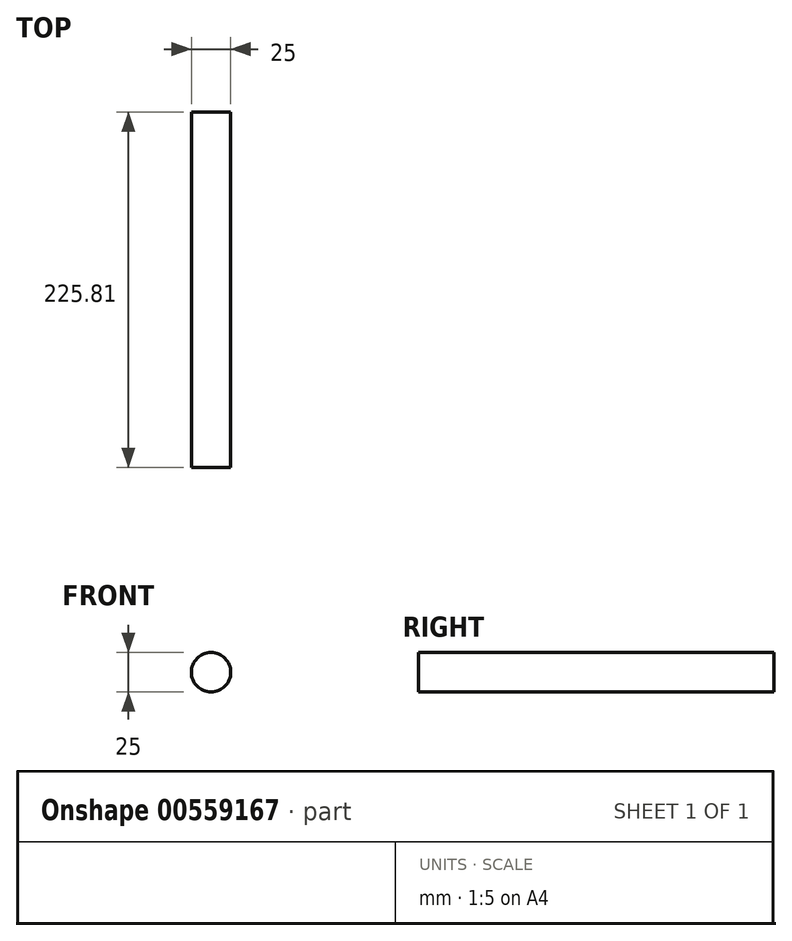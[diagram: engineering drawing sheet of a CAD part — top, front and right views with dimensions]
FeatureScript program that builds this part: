
annotation { "Feature Type Name" : "Feature", "Feature Type Description" : "" }
export const myFeature = defineFeature(function(context is Context, id is Id, definition is map)
    precondition{}
    {
        {
            var Q0;
            Q0=qCreatedBy(makeId("Front.planeOp"),FACE);
            var sketch = newSketch(context, id + "F0", { "sketchPlane" : qUnion([Q0])});
            skCircle(sketch, "E0", {"center": v(-125.22, 56.1) * mm, "radius": 12.5 * mm});
            skSolve(sketch);
        }
        {
            var Q0;
            Q0=makeQuery(id+"F0.imprint","IMPRINT",FACE,{"disambiguationData":[TD([[makeQuery(id+"F0.imprint","IMPRINT",EDGE,{"derivedFrom":sQuery(id+"F0.wireOp",EDGE,"E0")}),1.0]])]});
            extrude(context, id + "F1", {"entities" : qUnion([Q0]), "depth" : 225.8 * mm, "offsetDistance" : 25.4 * mm});
        }
        {
            var Q0;
            Q0=qCreatedBy(makeId("Right.planeOp"),FACE);
            var sketch = newSketch(context, id + "F2", { "sketchPlane" : qUnion([Q0])});
            skCircle(sketch, "E1", {"center": v(0, 0) * mm, "radius": 55 * mm});
            skSolve(sketch);
        }
        {
            var Q0;
            Q0=sQuery(id+"F2.wireOp",EDGE,"E1");
            extrude(context, id + "F3", {"bodyType" : ToolBodyType.SURFACE, "surfaceEntities" : qUnion([Q0]), "depth" : 152.4 * mm, "offsetDistance" : 25.4 * mm});
        }
    });
